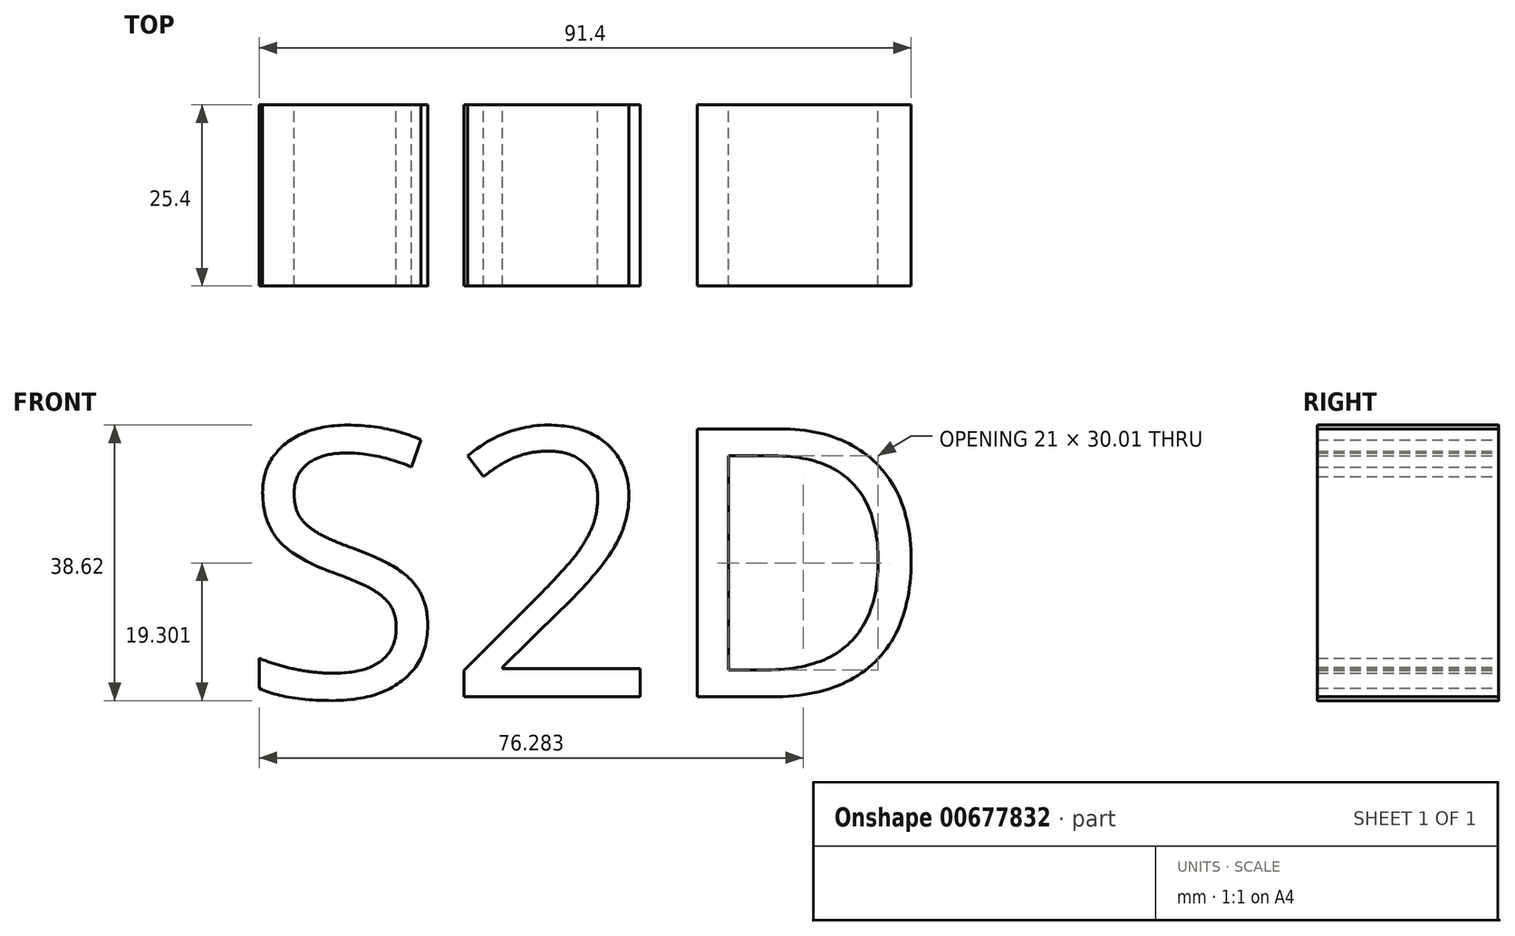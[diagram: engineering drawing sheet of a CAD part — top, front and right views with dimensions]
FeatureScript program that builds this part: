
annotation { "Feature Type Name" : "Feature", "Feature Type Description" : "" }
export const myFeature = defineFeature(function(context is Context, id is Id, definition is map)
    precondition{}
    {
        {
            var Q0;
            Q0=qCreatedBy(makeId("Front.planeOp"),FACE);
            var sketch = newSketch(context, id + "F0", { "sketchPlane" : qUnion([Q0])});
            skText(sketch, "E0", { "text": "S2D", "fontName": "OpenSans-Regular.ttf"});
            const initialGuessF0  = {"E0": [-0.04743, -0.01865, 1, 0, 0.03789]};
            skSetInitialGuess(sketch, initialGuessF0);
            skSolve(sketch);
        }
        {
            var Q0;
            Q0=makeQuery(id+"F0.imprint","IMPRINT",FACE,{"disambiguationData":[TD([[makeQuery(id+"F0.imprint","IMPRINT",EDGE,{"derivedFrom":sQuery(id+"F0.wireOp",EDGE,"E0.sketch_text.stroke-45")}),-1.0]])]});
            extrude(context, id + "F1", {"entities" : qUnion([Q0]), "endBound" : BoundingType.SYMMETRIC, "depth" : 25.4 * mm, "offsetDistance" : 25.4 * mm});
        }
        {
            var Q0;
            Q0 = qSketchRegion(id + "F0", true);
            extrude(context, id + "F2", {"entities" : qUnion([Q0]), "operationType" : NewBodyOperationType.ADD, "endBound" : BoundingType.SYMMETRIC, "depth" : 25.4 * mm, "offsetDistance" : 25.4 * mm});
        }
    });
